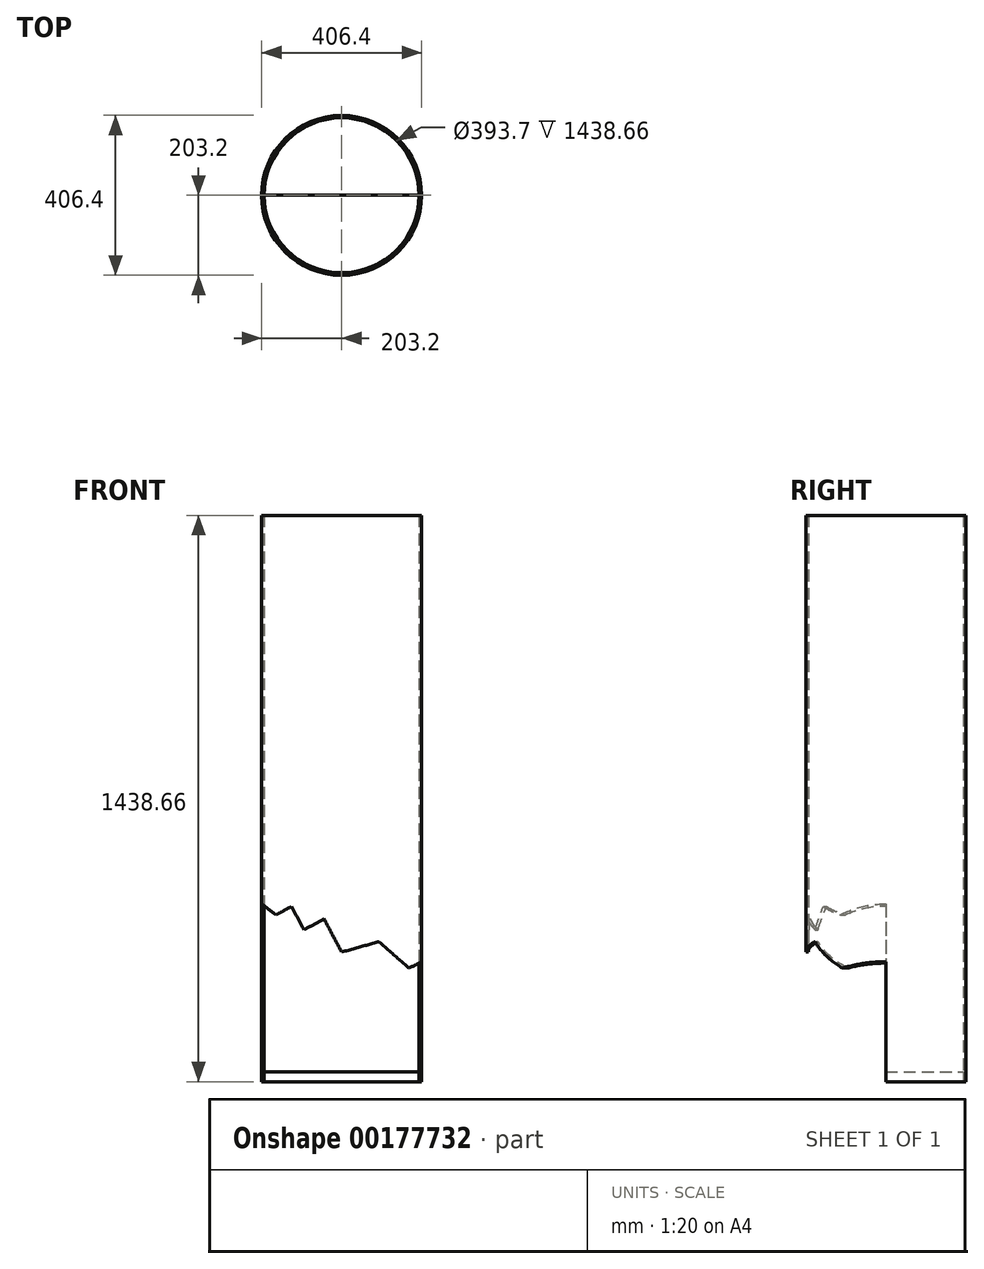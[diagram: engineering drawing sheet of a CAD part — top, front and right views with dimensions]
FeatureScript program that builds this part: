
annotation { "Feature Type Name" : "Feature", "Feature Type Description" : "" }
export const myFeature = defineFeature(function(context is Context, id is Id, definition is map)
    precondition{}
    {
        {
            var Q0;
            Q0=qCreatedBy(makeId("Top.planeOp"),FACE);
            var sketch = newSketch(context, id + "F0", { "sketchPlane" : qUnion([Q0])});
            skCircle(sketch, "E0", {"center": v(0, 0) * mm, "radius": 203.2 * mm});
            skCircle(sketch, "E1", {"center": v(0, 0) * mm, "radius": 196.85 * mm});
            skSolve(sketch);
        }
        {
            var Q0;
            Q0 = qSketchRegion(id + "F0", true);
            extrude(context, id + "F1", {"entities" : qUnion([Q0]), "depth" : 1438.66 * mm});
        }
        {
            var Q0;
            Q0=makeQuery(id+"F1.opExtrude","CAP_FACE",FACE,{"disambiguationData":[OSD([sQuery(id+"F0.wireOp",EDGE,"E0"),sQuery(id+"F0.wireOp",EDGE,"E1")])],"isStart":true});
            var sketch = newSketch(context, id + "F2", { "sketchPlane" : qUnion([Q0])});
            skCircle(sketch, "E2", {"center": v(0, 0) * mm, "radius": 196.85 * mm});
            skSolve(sketch);
        }
        {
            var Q0;
            Q0 = qSketchRegion(id + "F2", true);
            extrude(context, id + "F3", {"entities" : qUnion([Q0]), "oppositeDirection" : true, "depth" : 25.4 * mm});
        }
        {
            var Q0;
            Q0=qCreatedBy(makeId("Front.planeOp"),FACE);
            var sketch = newSketch(context, id + "F4", { "sketchPlane" : qUnion([Q0])});
            skLineSegment(sketch, "E3", {"start": v(-262.2, -27.54) * mm, "end": v(319.67, -27.54) * mm});
            skLineSegment(sketch, "E4", {"start": v(319.67, -27.54) * mm, "end": v(319.67, 288.54) * mm});
            skLineSegment(sketch, "E5", {"start": v(319.67, 288.54) * mm, "end": v(228.67, 317.27) * mm});
            skLineSegment(sketch, "E6", {"start": v(228.67, 317.27) * mm, "end": v(171.2, 288.54) * mm});
            skLineSegment(sketch, "E7", {"start": v(171.2, 288.54) * mm, "end": v(94.58, 355.58) * mm});
            skLineSegment(sketch, "E8", {"start": v(94.58, 355.58) * mm, "end": v(0, 329.24) * mm});
            skLineSegment(sketch, "E9", {"start": v(0, 329.24) * mm, "end": v(-44.3, 413.05) * mm});
            skLineSegment(sketch, "E10", {"start": v(-44.3, 413.05) * mm, "end": v(-95.69, 385.89) * mm});
            skLineSegment(sketch, "E11", {"start": v(-95.69, 385.89) * mm, "end": v(-126.96, 445.06) * mm});
            skLineSegment(sketch, "E12", {"start": v(-126.96, 445.06) * mm, "end": v(-167.17, 423.8) * mm});
            skLineSegment(sketch, "E13", {"start": v(-167.17, 423.8) * mm, "end": v(-233.46, 475.3) * mm});
            skLineSegment(sketch, "E14", {"start": v(-233.46, 475.3) * mm, "end": v(-262.2, -27.54) * mm});
            skSolve(sketch);
        }
        {
            var Q0;
            Q0 = qSketchRegion(id + "F4", true);
            extrude(context, id + "F5", {"entities" : qUnion([Q0]), "operationType" : NewBodyOperationType.REMOVE, "depth" : 508 * mm});
        }
    });
